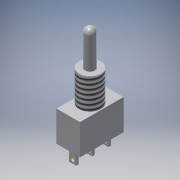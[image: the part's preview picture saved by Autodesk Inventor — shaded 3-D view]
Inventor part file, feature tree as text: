
AUTODESK INVENTOR PART (.ipt)
format: ipt  version: 2016 (Build 200138000, 138)  size: 160,256 bytes
history: native  units: mm
features: sketch x8, extrude x5, fillet x1, thread x1
ambient origin geometry x8: Origin, YZ Plane, XZ Plane, XY Plane, X Axis, Y Axis, Z Axis, Center Point
bodies: Solid1 (feature_tree)
feature tree (15):
  extrude  "Extrusion1"  Depth=12.7mm
  extrude  "Extrusion2"  Depth=8.89mm TaperAngle=0.0deg
  extrude  "Extrusion3"  Depth=0.76mm
  extrude  "Extrusion4"  Depth=4.7mm
  extrude  "Extrusion5"  Depth=3.96mm
  fillet  "Fillet1"  Radius=1.0mm
  thread  "Thread1"  [1 undecoded]
  sketch  "Sketch7"  dims[d27=3.96mm d28=0.0mm]
  sketch  "Sketch8"  dims[d29=2.92mm]
  sketch  "Sketch9"  dims[d30=10.41mm d31=0.0mm d32=1.46mm d33=10.0mm d34=0.0mm d35=6.35mm]
  sketch  "Sketch1"  dims[d0=6.86mm d1=12.7mm]
  sketch  "Sketch2"  dims[d2=8.89mm d3=0.0mm d4=8.89mm d5=0.0mm]
  sketch  "Sketch3"  dims[d6=2.03mm d7=0.76mm]
  sketch  "Sketch4"  dims[d8=30.0mm d10=4.7mm d11=10.0mm d13=10.0mm d15=20.0mm d17=4.7mm d18=10.0mm d20=10.0mm]
  sketch  "Sketch6"  dims[d22=3.96mm d23=0.0mm d24=1.0mm d25=1.0mm d26=1.015mm]
note: 1 required parameter value undecoded (feature->parameter linkage not recoverable at this tier; creation-order binding heuristic only, values carry confidence <= 0.55)
